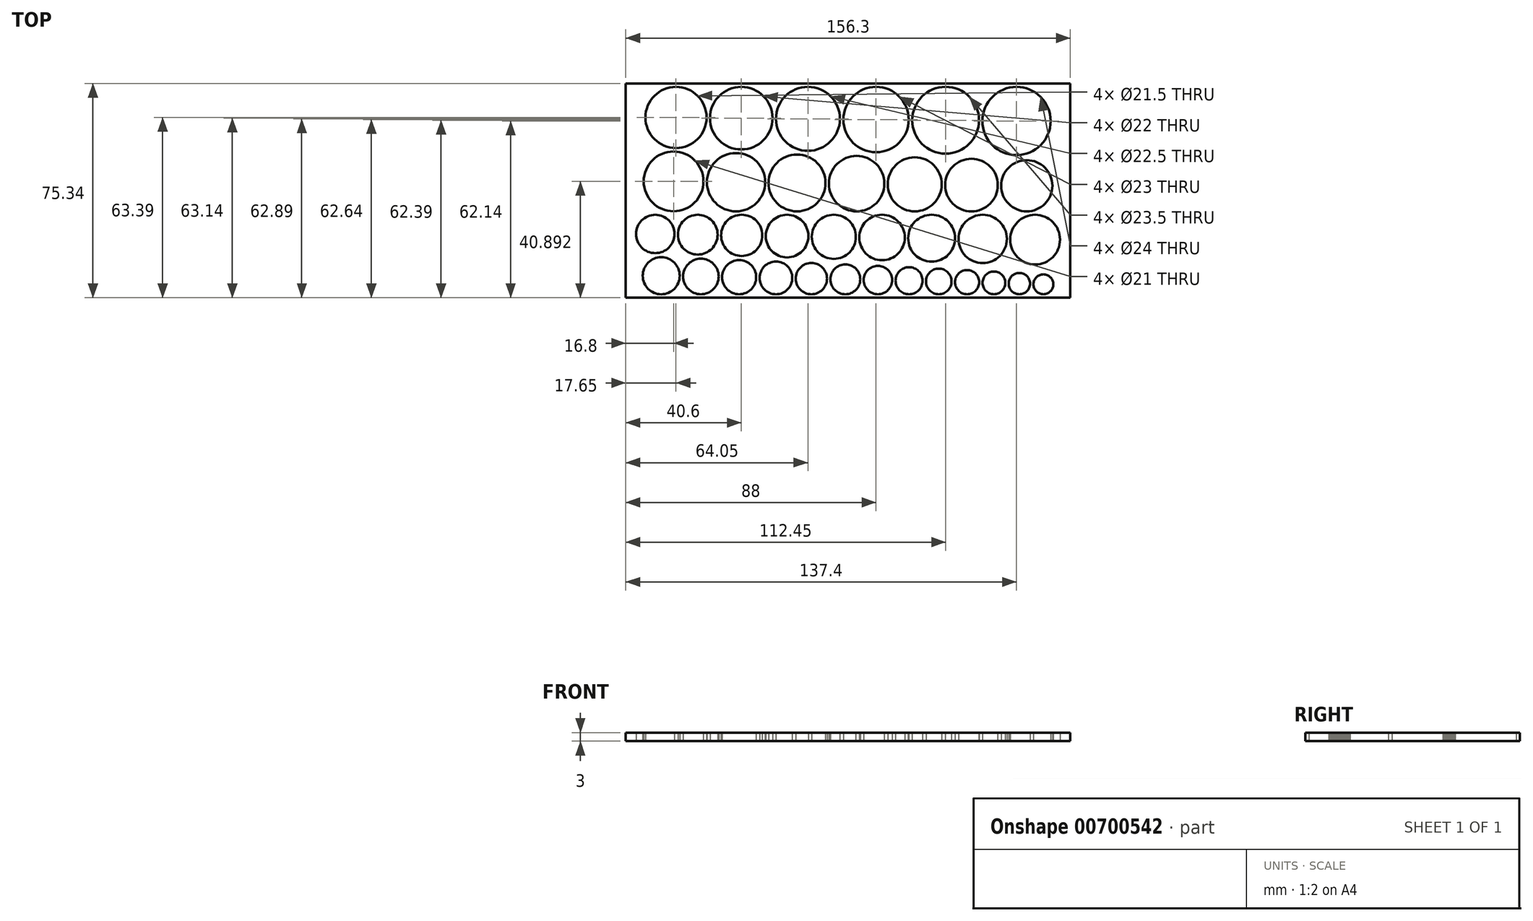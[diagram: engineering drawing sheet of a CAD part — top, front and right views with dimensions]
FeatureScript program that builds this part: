
annotation { "Feature Type Name" : "Feature", "Feature Type Description" : "" }
export const myFeature = defineFeature(function(context is Context, id is Id, definition is map)
    precondition{}
    {
        {
            var Q0;
            Q0=qCreatedBy(makeId("Top.planeOp"),FACE);
            var sketch = newSketch(context, id + "F0", { "sketchPlane" : qUnion([Q0])});
            skLineSegment(sketch, "E0.bottom", {"start": v(-156.3, 0) * mm, "end": v(0, 0) * mm});
            skLineSegment(sketch, "E0.top", {"start": v(-156.3, -75.34) * mm, "end": v(0, -75.34) * mm});
            skLineSegment(sketch, "E0.left", {"start": v(-156.3, 0) * mm, "end": v(-156.3, -75.34) * mm});
            skLineSegment(sketch, "E0.right", {"start": v(0, 0) * mm, "end": v(0, -75.34) * mm});
            skCircle(sketch, "E1", {"center": v(-54.7, -35.48) * mm, "radius": 9.5 * mm});
            skCircle(sketch, "E2", {"center": v(-34.75, -35.73) * mm, "radius": 9.25 * mm});
            skCircle(sketch, "E3", {"center": v(-15.3, -35.98) * mm, "radius": 9 * mm});
            skCircle(sketch, "E4", {"center": v(-30.8, -54.68) * mm, "radius": 8.5 * mm});
            skCircle(sketch, "E5", {"center": v(-48.75, -54.43) * mm, "radius": 8.25 * mm});
            skCircle(sketch, "E6", {"center": v(-66.2, -54.18) * mm, "radius": 8 * mm});
            skCircle(sketch, "E7", {"center": v(-83.15, -53.93) * mm, "radius": 7.75 * mm});
            skCircle(sketch, "E8", {"center": v(-99.6, -53.68) * mm, "radius": 7.5 * mm});
            skCircle(sketch, "E9", {"center": v(-115.55, -53.43) * mm, "radius": 7.25 * mm});
            skCircle(sketch, "E10", {"center": v(-131, -53.18) * mm, "radius": 7 * mm});
            skCircle(sketch, "E11", {"center": v(-145.95, -52.93) * mm, "radius": 6.75 * mm});
            skCircle(sketch, "E12", {"center": v(-103.5, -68.4) * mm, "radius": 5.75 * mm});
            skCircle(sketch, "E13", {"center": v(-91.05, -68.64) * mm, "radius": 5.5 * mm});
            skCircle(sketch, "E14", {"center": v(-79.1, -68.9) * mm, "radius": 5.25 * mm});
            skCircle(sketch, "E15", {"center": v(-67.65, -69.14) * mm, "radius": 5 * mm});
            skCircle(sketch, "E16", {"center": v(-56.7, -69.4) * mm, "radius": 4.75 * mm});
            skCircle(sketch, "E17", {"center": v(-46.25, -69.64) * mm, "radius": 4.5 * mm});
            skCircle(sketch, "E18", {"center": v(-36.3, -69.9) * mm, "radius": 4.25 * mm});
            skCircle(sketch, "E19", {"center": v(-26.85, -70.14) * mm, "radius": 4 * mm});
            skCircle(sketch, "E20", {"center": v(-17.9, -70.4) * mm, "radius": 3.75 * mm});
            skCircle(sketch, "E21", {"center": v(-9.45, -70.64) * mm, "radius": 3.5 * mm});
            skCircle(sketch, "E22", {"center": v(-75.15, -35.23) * mm, "radius": 9.75 * mm});
            skCircle(sketch, "E23", {"center": v(-138.65, -11.95) * mm, "radius": 10.75 * mm});
            skCircle(sketch, "E24", {"center": v(-115.7, -12.2) * mm, "radius": 11 * mm});
            skCircle(sketch, "E25", {"center": v(-92.25, -12.45) * mm, "radius": 11.25 * mm});
            skCircle(sketch, "E26", {"center": v(-68.3, -12.7) * mm, "radius": 11.5 * mm});
            skCircle(sketch, "E27", {"center": v(-43.85, -12.95) * mm, "radius": 11.75 * mm});
            skCircle(sketch, "E28", {"center": v(-18.9, -13.2) * mm, "radius": 12 * mm});
            skLineSegment(sketch, "E29", {"start": v(0, -1.2) * mm, "end": v(-156.3, -1.2) * mm, "construction": true});
            skLineSegment(sketch, "E30", {"start": v(0, -74.14) * mm, "end": v(0, -75.34) * mm, "construction": true});
            skLineSegment(sketch, "E31", {"start": v(0, -1.2) * mm, "end": v(0, 0) * mm, "construction": true});
            skLineSegment(sketch, "E32", {"start": v(-1.2, -75.34) * mm, "end": v(-1.2, 0) * mm, "construction": true});
            skLineSegment(sketch, "E33", {"start": v(-1.2, 0) * mm, "end": v(0, 0) * mm, "construction": true});
            skLineSegment(sketch, "E34", {"start": v(-155.1, -75.34) * mm, "end": v(-155.1, 0) * mm, "construction": true});
            skLineSegment(sketch, "E35", {"start": v(-156.3, 0) * mm, "end": v(-155.1, 0) * mm, "construction": true});
            skLineSegment(sketch, "E36", {"start": v(-30.9, -13.2) * mm, "end": v(-30.9, -1.2) * mm, "construction": true});
            skLineSegment(sketch, "E37", {"start": v(-30.9, -1.2) * mm, "end": v(-32.1, -1.2) * mm, "construction": true});
            skLineSegment(sketch, "E38", {"start": v(-32.1, -1.2) * mm, "end": v(-32.1, -12.95) * mm, "construction": true});
            skLineSegment(sketch, "E39", {"start": v(-55.6, -12.95) * mm, "end": v(-55.6, -1.2) * mm, "construction": true});
            skLineSegment(sketch, "E40", {"start": v(-55.6, -1.2) * mm, "end": v(-56.8, -1.2) * mm, "construction": true});
            skLineSegment(sketch, "E41", {"start": v(-56.8, -1.2) * mm, "end": v(-56.8, -12.7) * mm, "construction": true});
            skLineSegment(sketch, "E42", {"start": v(-79.8, -12.7) * mm, "end": v(-79.8, -1.2) * mm, "construction": true});
            skLineSegment(sketch, "E43", {"start": v(-79.8, -1.2) * mm, "end": v(-81, -1.2) * mm, "construction": true});
            skLineSegment(sketch, "E44", {"start": v(-81, -1.2) * mm, "end": v(-81, -12.45) * mm, "construction": true});
            skLineSegment(sketch, "E45", {"start": v(-103.5, -12.45) * mm, "end": v(-103.5, -1.2) * mm, "construction": true});
            skLineSegment(sketch, "E46", {"start": v(-103.5, -1.2) * mm, "end": v(-104.7, -1.2) * mm, "construction": true});
            skLineSegment(sketch, "E47", {"start": v(-104.7, -1.2) * mm, "end": v(-104.7, -12.2) * mm, "construction": true});
            skLineSegment(sketch, "E48", {"start": v(-126.7, -12.2) * mm, "end": v(-126.7, -1.2) * mm, "construction": true});
            skLineSegment(sketch, "E49", {"start": v(-126.7, -1.2) * mm, "end": v(-127.9, -1.2) * mm, "construction": true});
            skLineSegment(sketch, "E50", {"start": v(-127.9, -1.2) * mm, "end": v(-127.9, -11.95) * mm, "construction": true});
            skCircle(sketch, "E51", {"center": v(-117.55, -34.73) * mm, "radius": 10.25 * mm});
            skCircle(sketch, "E52", {"center": v(-96.1, -34.98) * mm, "radius": 10 * mm});
            skLineSegment(sketch, "E53", {"start": v(-156.3, -44.98) * mm, "end": v(0, -44.98) * mm, "construction": true});
            skLineSegment(sketch, "E54", {"start": v(-107.3, -34.73) * mm, "end": v(-107.3, -44.98) * mm, "construction": true});
            skLineSegment(sketch, "E55", {"start": v(-107.3, -44.98) * mm, "end": v(-106.1, -44.98) * mm, "construction": true});
            skLineSegment(sketch, "E56", {"start": v(-106.1, -44.98) * mm, "end": v(-106.1, -34.98) * mm, "construction": true});
            skLineSegment(sketch, "E57", {"start": v(-86.1, -34.98) * mm, "end": v(-86.1, -44.98) * mm, "construction": true});
            skLineSegment(sketch, "E58", {"start": v(-86.1, -44.98) * mm, "end": v(-84.9, -44.98) * mm, "construction": true});
            skLineSegment(sketch, "E59", {"start": v(-84.9, -44.98) * mm, "end": v(-84.9, -35.23) * mm, "construction": true});
            skLineSegment(sketch, "E60", {"start": v(-65.4, -35.23) * mm, "end": v(-65.4, -44.98) * mm, "construction": true});
            skLineSegment(sketch, "E61", {"start": v(-65.4, -44.98) * mm, "end": v(-64.2, -44.98) * mm, "construction": true});
            skLineSegment(sketch, "E62", {"start": v(-64.2, -44.98) * mm, "end": v(-64.2, -35.48) * mm, "construction": true});
            skLineSegment(sketch, "E63", {"start": v(-45.2, -35.48) * mm, "end": v(-45.2, -44.98) * mm, "construction": true});
            skLineSegment(sketch, "E64", {"start": v(-45.2, -44.98) * mm, "end": v(-44, -44.98) * mm, "construction": true});
            skLineSegment(sketch, "E65", {"start": v(-44, -44.98) * mm, "end": v(-44, -35.73) * mm, "construction": true});
            skLineSegment(sketch, "E66", {"start": v(-24.3, -35.98) * mm, "end": v(-24.3, -44.98) * mm, "construction": true});
            skLineSegment(sketch, "E67", {"start": v(-24.3, -44.98) * mm, "end": v(-25.5, -44.98) * mm, "construction": true});
            skLineSegment(sketch, "E68", {"start": v(-25.5, -44.98) * mm, "end": v(-25.5, -35.73) * mm, "construction": true});
            skLineSegment(sketch, "E69", {"start": v(-6.3, -35.98) * mm, "end": v(-1.2, -35.98) * mm, "construction": true});
            skLineSegment(sketch, "E70", {"start": v(0, -25.6) * mm, "end": v(-156.3, -22.33) * mm, "construction": true});
            skLineSegment(sketch, "E71", {"start": v(-156.3, -23.53) * mm, "end": v(0, -27.36) * mm, "construction": true});
            skLineSegment(sketch, "E72", {"start": v(0, -46.18) * mm, "end": v(-156.3, -46.18) * mm, "construction": true});
            skLineSegment(sketch, "E73", {"start": v(-156.3, -46.18) * mm, "end": v(-156.3, -44.98) * mm, "construction": true});
            skLineSegment(sketch, "E74", {"start": v(-57, -54.43) * mm, "end": v(-57, -46.18) * mm, "construction": true});
            skLineSegment(sketch, "E75", {"start": v(-57, -46.18) * mm, "end": v(-58.2, -46.18) * mm, "construction": true});
            skLineSegment(sketch, "E76", {"start": v(-58.2, -46.18) * mm, "end": v(-58.2, -54.18) * mm, "construction": true});
            skLineSegment(sketch, "E77", {"start": v(-74.2, -54.18) * mm, "end": v(-74.2, -46.18) * mm, "construction": true});
            skLineSegment(sketch, "E78", {"start": v(-74.2, -46.18) * mm, "end": v(-75.4, -46.18) * mm, "construction": true});
            skLineSegment(sketch, "E79", {"start": v(-75.4, -46.18) * mm, "end": v(-75.4, -53.93) * mm, "construction": true});
            skLineSegment(sketch, "E80", {"start": v(-90.9, -53.93) * mm, "end": v(-90.9, -46.18) * mm, "construction": true});
            skLineSegment(sketch, "E81", {"start": v(-90.9, -46.18) * mm, "end": v(-92.1, -46.18) * mm, "construction": true});
            skLineSegment(sketch, "E82", {"start": v(-92.1, -46.18) * mm, "end": v(-92.1, -53.68) * mm, "construction": true});
            skLineSegment(sketch, "E83", {"start": v(-107.1, -53.68) * mm, "end": v(-107.1, -46.18) * mm, "construction": true});
            skLineSegment(sketch, "E84", {"start": v(-107.1, -46.18) * mm, "end": v(-108.3, -46.18) * mm, "construction": true});
            skLineSegment(sketch, "E85", {"start": v(-108.3, -46.18) * mm, "end": v(-108.3, -53.43) * mm, "construction": true});
            skLineSegment(sketch, "E86", {"start": v(-122.8, -53.43) * mm, "end": v(-122.8, -46.18) * mm, "construction": true});
            skLineSegment(sketch, "E87", {"start": v(-122.8, -46.18) * mm, "end": v(-124, -46.18) * mm, "construction": true});
            skLineSegment(sketch, "E88", {"start": v(-124, -46.18) * mm, "end": v(-124, -53.18) * mm, "construction": true});
            skLineSegment(sketch, "E89", {"start": v(-138, -53.18) * mm, "end": v(-138, -46.18) * mm, "construction": true});
            skLineSegment(sketch, "E90", {"start": v(-138, -46.18) * mm, "end": v(-139.2, -46.18) * mm, "construction": true});
            skLineSegment(sketch, "E91", {"start": v(-139.2, -46.18) * mm, "end": v(-139.2, -52.93) * mm, "construction": true});
            skLineSegment(sketch, "E92", {"start": v(-152.7, -52.93) * mm, "end": v(-155.1, -52.93) * mm, "construction": true});
            skLineSegment(sketch, "E93", {"start": v(-3.6, -54.93) * mm, "end": v(-1.2, -54.93) * mm, "construction": true});
            skLineSegment(sketch, "E94", {"start": v(-97.75, -68.4) * mm, "end": v(-97.75, -69.6) * mm, "construction": true});
            skLineSegment(sketch, "E95", {"start": v(-97.75, -69.6) * mm, "end": v(-96.55, -69.6) * mm, "construction": true});
            skLineSegment(sketch, "E96", {"start": v(-85.55, -68.64) * mm, "end": v(-85.55, -69.84) * mm, "construction": true});
            skLineSegment(sketch, "E97", {"start": v(-85.55, -69.84) * mm, "end": v(-84.35, -69.84) * mm, "construction": true});
            skLineSegment(sketch, "E98", {"start": v(-84.35, -69.84) * mm, "end": v(-84.35, -68.9) * mm, "construction": true});
            skLineSegment(sketch, "E99", {"start": v(-73.85, -68.9) * mm, "end": v(-73.85, -70.1) * mm, "construction": true});
            skLineSegment(sketch, "E100", {"start": v(-73.85, -70.1) * mm, "end": v(-72.65, -70.1) * mm, "construction": true});
            skLineSegment(sketch, "E101", {"start": v(-72.65, -70.1) * mm, "end": v(-72.65, -69.14) * mm, "construction": true});
            skLineSegment(sketch, "E102", {"start": v(-62.65, -69.14) * mm, "end": v(-62.65, -70.34) * mm, "construction": true});
            skLineSegment(sketch, "E103", {"start": v(-62.65, -70.34) * mm, "end": v(-61.45, -70.34) * mm, "construction": true});
            skLineSegment(sketch, "E104", {"start": v(-61.45, -70.34) * mm, "end": v(-61.45, -69.4) * mm, "construction": true});
            skLineSegment(sketch, "E105", {"start": v(-51.95, -69.4) * mm, "end": v(-51.95, -70.6) * mm, "construction": true});
            skLineSegment(sketch, "E106", {"start": v(-51.95, -70.6) * mm, "end": v(-50.75, -70.6) * mm, "construction": true});
            skLineSegment(sketch, "E107", {"start": v(-50.75, -70.6) * mm, "end": v(-50.75, -69.64) * mm, "construction": true});
            skLineSegment(sketch, "E108", {"start": v(-41.75, -69.64) * mm, "end": v(-41.75, -70.84) * mm, "construction": true});
            skLineSegment(sketch, "E109", {"start": v(-41.75, -70.84) * mm, "end": v(-40.55, -70.84) * mm, "construction": true});
            skLineSegment(sketch, "E110", {"start": v(-40.55, -70.84) * mm, "end": v(-40.55, -69.9) * mm, "construction": true});
            skLineSegment(sketch, "E111", {"start": v(-32.05, -69.9) * mm, "end": v(-32.05, -71.1) * mm, "construction": true});
            skLineSegment(sketch, "E112", {"start": v(-32.05, -71.1) * mm, "end": v(-30.85, -71.1) * mm, "construction": true});
            skLineSegment(sketch, "E113", {"start": v(-30.85, -71.1) * mm, "end": v(-30.85, -70.14) * mm, "construction": true});
            skLineSegment(sketch, "E114", {"start": v(-22.85, -70.14) * mm, "end": v(-22.85, -71.34) * mm, "construction": true});
            skLineSegment(sketch, "E115", {"start": v(-22.85, -71.34) * mm, "end": v(-21.65, -71.34) * mm, "construction": true});
            skLineSegment(sketch, "E116", {"start": v(-21.65, -71.34) * mm, "end": v(-21.65, -70.4) * mm, "construction": true});
            skLineSegment(sketch, "E117", {"start": v(-14.15, -70.4) * mm, "end": v(-14.15, -71.6) * mm, "construction": true});
            skLineSegment(sketch, "E118", {"start": v(-14.15, -71.6) * mm, "end": v(-12.95, -71.6) * mm, "construction": true});
            skLineSegment(sketch, "E119", {"start": v(-12.95, -71.6) * mm, "end": v(-12.95, -70.64) * mm, "construction": true});
            skLineSegment(sketch, "E120", {"start": v(-96.55, -69.6) * mm, "end": v(-96.55, -68.64) * mm, "construction": true});
            skCircle(sketch, "E121", {"center": v(-116.45, -68.14) * mm, "radius": 6 * mm});
            skCircle(sketch, "E122", {"center": v(-129.9, -67.9) * mm, "radius": 6.25 * mm});
            skLineSegment(sketch, "E123", {"start": v(-123.65, -67.9) * mm, "end": v(-123.65, -69.1) * mm, "construction": true});
            skLineSegment(sketch, "E124", {"start": v(-123.65, -69.1) * mm, "end": v(-122.45, -69.1) * mm, "construction": true});
            skLineSegment(sketch, "E125", {"start": v(-122.45, -69.1) * mm, "end": v(-122.45, -68.14) * mm, "construction": true});
            skLineSegment(sketch, "E126", {"start": v(-110.45, -68.14) * mm, "end": v(-110.45, -69.34) * mm, "construction": true});
            skLineSegment(sketch, "E127", {"start": v(-110.45, -69.34) * mm, "end": v(-109.25, -69.34) * mm, "construction": true});
            skLineSegment(sketch, "E128", {"start": v(-109.25, -69.34) * mm, "end": v(-109.25, -68.4) * mm, "construction": true});
            skLineSegment(sketch, "E129", {"start": v(-39.3, -55.88) * mm, "end": v(-39.3, -54.68) * mm, "construction": true});
            skLineSegment(sketch, "E130", {"start": v(-39.3, -55.88) * mm, "end": v(-40.5, -55.88) * mm, "construction": true});
            skLineSegment(sketch, "E131", {"start": v(-40.5, -54.43) * mm, "end": v(-40.5, -55.88) * mm, "construction": true});
            skLineSegment(sketch, "E132", {"start": v(-5.95, -70.64) * mm, "end": v(-1.2, -70.64) * mm, "construction": true});
            skLineSegment(sketch, "E133", {"start": v(-155.1, -67.64) * mm, "end": v(-150.35, -67.64) * mm, "construction": true});
            skLineSegment(sketch, "E134", {"start": v(0, -64.06) * mm, "end": v(-156.3, -59.38) * mm, "construction": true});
            skCircle(sketch, "E135", {"center": v(-139.5, -34.45) * mm, "radius": 10.5 * mm});
            skCircle(sketch, "E136", {"center": v(-12.35, -54.93) * mm, "radius": 8.75 * mm});
            skCircle(sketch, "E137", {"center": v(-143.85, -67.64) * mm, "radius": 6.5 * mm});
            skLineSegment(sketch, "E138", {"start": v(-129, -34.45) * mm, "end": v(-129, -35.65) * mm, "construction": true});
            skLineSegment(sketch, "E139", {"start": v(-129, -35.65) * mm, "end": v(-127.8, -35.65) * mm, "construction": true});
            skLineSegment(sketch, "E140", {"start": v(-127.8, -35.65) * mm, "end": v(-127.8, -34.73) * mm, "construction": true});
            skLineSegment(sketch, "E141", {"start": v(-150, -34.45) * mm, "end": v(-155.1, -34.45) * mm, "construction": true});
            skLineSegment(sketch, "E142", {"start": v(-21.1, -54.93) * mm, "end": v(-21.1, -53.73) * mm, "construction": true});
            skLineSegment(sketch, "E143", {"start": v(-21.1, -53.73) * mm, "end": v(-22.3, -53.73) * mm, "construction": true});
            skLineSegment(sketch, "E144", {"start": v(-22.3, -53.73) * mm, "end": v(-22.3, -54.68) * mm, "construction": true});
            skLineSegment(sketch, "E145", {"start": v(-137.35, -67.64) * mm, "end": v(-137.35, -68.84) * mm, "construction": true});
            skLineSegment(sketch, "E146", {"start": v(-137.35, -68.84) * mm, "end": v(-136.15, -68.84) * mm, "construction": true});
            skLineSegment(sketch, "E147", {"start": v(-136.15, -68.84) * mm, "end": v(-136.15, -67.9) * mm, "construction": true});
            skLineSegment(sketch, "E148", {"start": v(0, -74.14) * mm, "end": v(-156.3, -74.14) * mm, "construction": true});
            skLineSegment(sketch, "E149", {"start": v(-156.3, -60.58) * mm, "end": v(0, -67.56) * mm, "construction": true});
            skLineSegment(sketch, "E150", {"start": v(-6.9, -13.2) * mm, "end": v(-1.2, -13.2) * mm, "construction": true});
            skLineSegment(sketch, "E151", {"start": v(-149.4, -11.95) * mm, "end": v(-155.1, -11.95) * mm, "construction": true});
            skLineSegment(sketch, "E152", {"start": v(-156.3, -22.33) * mm, "end": v(-156.3, -23.53) * mm, "construction": true});
            skLineSegment(sketch, "E153", {"start": v(-156.3, -60.58) * mm, "end": v(-156.3, -59.38) * mm, "construction": true});
            skSolve(sketch);
        }
        {
            var Q0;
            Q0=makeQuery(id+"F0.imprint","IMPRINT",FACE,{"disambiguationData":[TD([[makeQuery(id+"F0.imprint","IMPRINT",EDGE,{"derivedFrom":sQuery(id+"F0.wireOp",EDGE,"E0.bottom")}),-1.0]])]});
            extrude(context, id + "F1", {"entities" : qUnion([Q0]), "depth" : 3 * mm, "offsetDistance" : 25 * mm});
        }
    });
